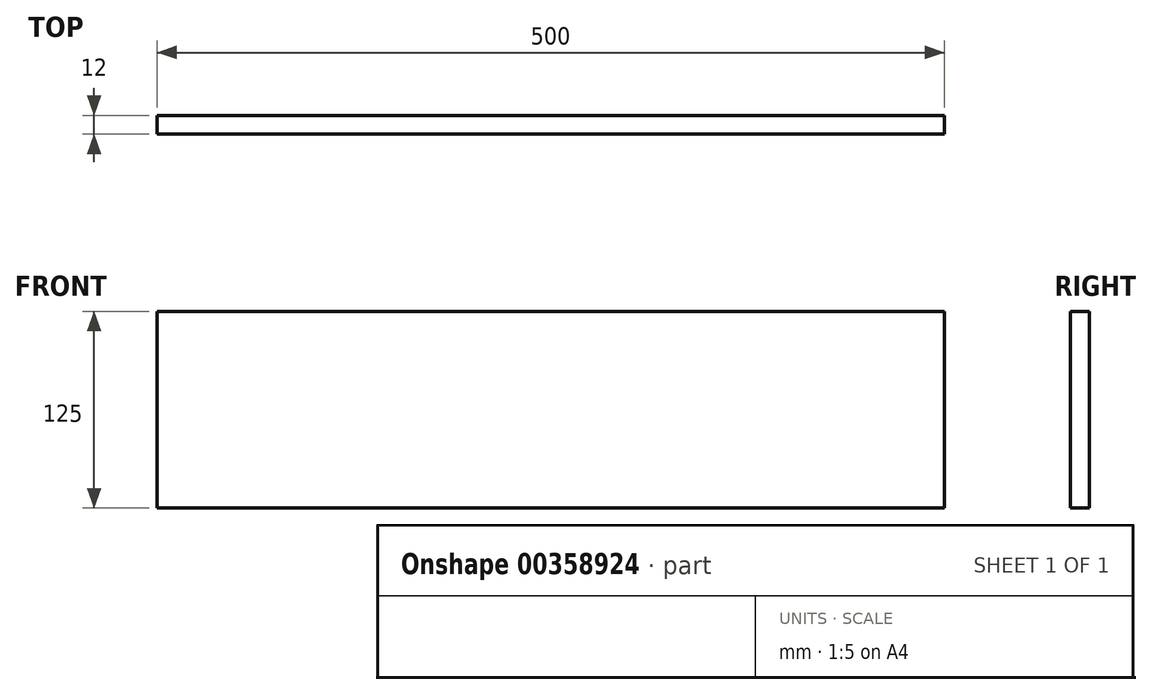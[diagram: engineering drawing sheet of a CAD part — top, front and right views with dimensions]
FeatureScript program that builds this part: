
annotation { "Feature Type Name" : "Feature", "Feature Type Description" : "" }
export const myFeature = defineFeature(function(context is Context, id is Id, definition is map)
    precondition{}
    {
        {
            var Q0;
            Q0=qCreatedBy(makeId("Front.planeOp"),FACE);
            var sketch = newSketch(context, id + "F0", { "sketchPlane" : qUnion([Q0])});
            skLineSegment(sketch, "E0.bottom", {"start": v(-250, 0) * mm, "end": v(250, 0) * mm});
            skLineSegment(sketch, "E0.top", {"start": v(-250, 125) * mm, "end": v(250, 125) * mm});
            skLineSegment(sketch, "E0.left", {"start": v(-250, 0) * mm, "end": v(-250, 125) * mm});
            skLineSegment(sketch, "E0.right", {"start": v(250, 0) * mm, "end": v(250, 125) * mm});
            skSolve(sketch);
        }
        {
            var Q0;
            Q0 = qSketchRegion(id + "F0", true);
            extrude(context, id + "F1", {"entities" : qUnion([Q0]), "depth" : 12 * mm});
        }
    });
